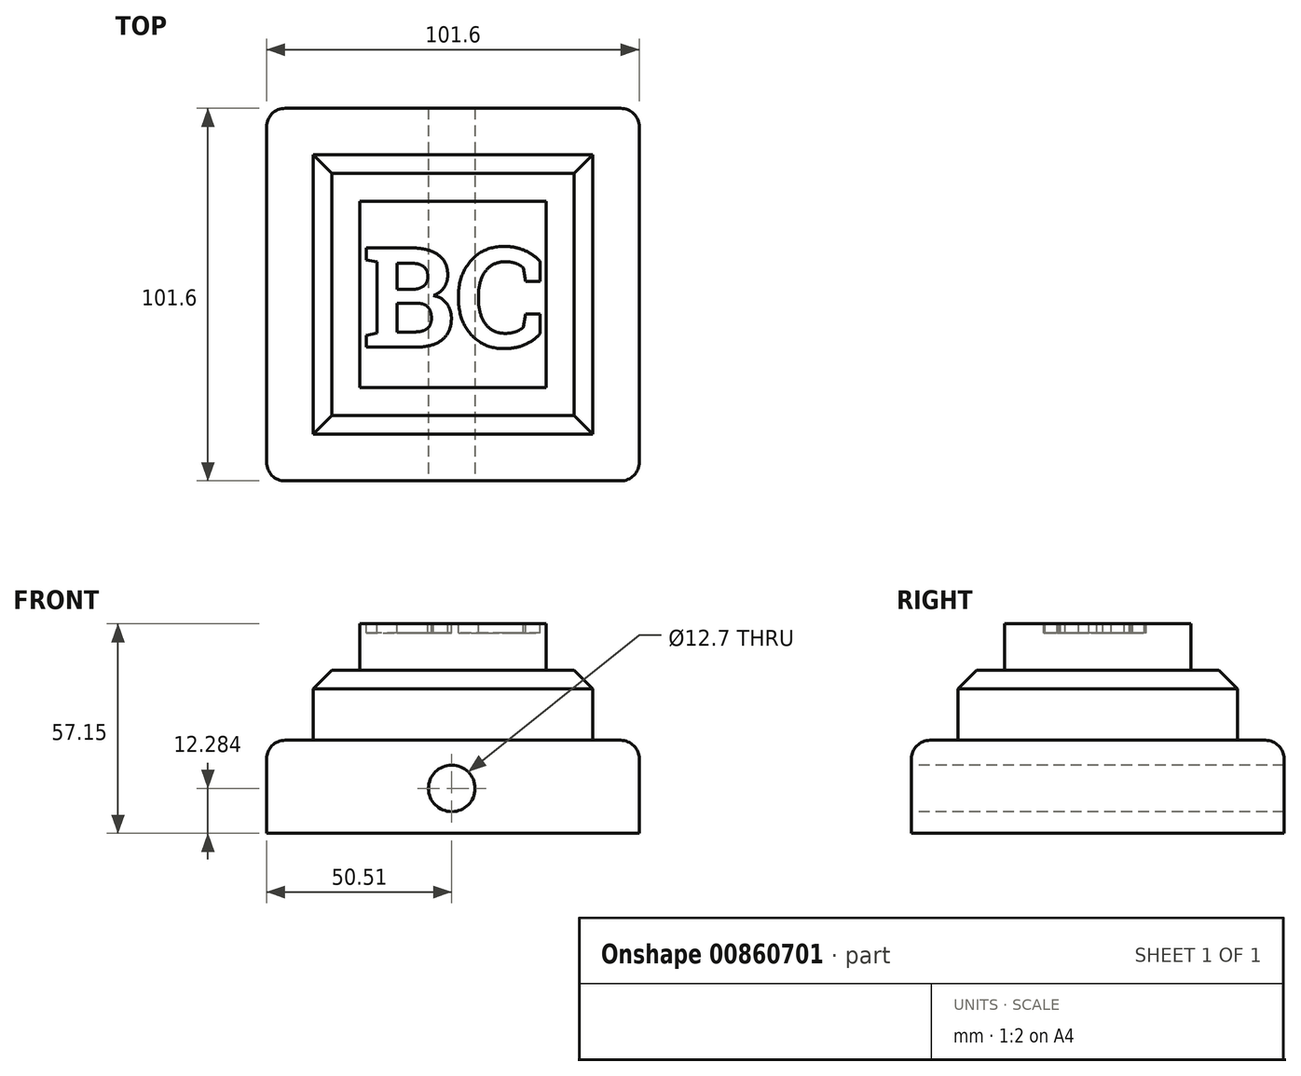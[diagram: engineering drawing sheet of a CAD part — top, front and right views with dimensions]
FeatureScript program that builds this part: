
annotation { "Feature Type Name" : "Feature", "Feature Type Description" : "" }
export const myFeature = defineFeature(function(context is Context, id is Id, definition is map)
    precondition{}
    {
        {
            var Q0;
            Q0=qCreatedBy(makeId("Top.planeOp"),FACE);
            var sketch = newSketch(context, id + "F0", { "sketchPlane" : qUnion([Q0])});
            skLineSegment(sketch, "E0.bottom", {"start": v(0, 0) * mm, "end": v(-101.6, 0) * mm});
            skLineSegment(sketch, "E0.top", {"start": v(0, 101.6) * mm, "end": v(-101.6, 101.6) * mm});
            skLineSegment(sketch, "E0.left", {"start": v(0, 0) * mm, "end": v(0, 101.6) * mm});
            skLineSegment(sketch, "E0.right", {"start": v(-101.6, 0) * mm, "end": v(-101.6, 101.6) * mm});
            skSolve(sketch);
        }
        {
            var Q0;
            Q0=makeQuery(id+"F0.imprint","IMPRINT",FACE,{"disambiguationData":[TD([[makeQuery(id+"F0.imprint","IMPRINT",EDGE,{"derivedFrom":sQuery(id+"F0.wireOp",EDGE,"E0.bottom")}),-1.0]])]});
            extrude(context, id + "F1", {"entities" : qUnion([Q0]), "depth" : 25.4 * mm, "offsetDistance" : 25.4 * mm});
        }
        {
            var Q0;
            Q0=makeQuery(id+"F1.opExtrude","CAP_FACE",FACE,{"disambiguationData":[OSD([sQuery(id+"F0.wireOp",EDGE,"E0.bottom"),sQuery(id+"F0.wireOp",EDGE,"E0.top"),sQuery(id+"F0.wireOp",EDGE,"E0.left"),sQuery(id+"F0.wireOp",EDGE,"E0.right")])],"isStart":false});
            var sketch = newSketch(context, id + "F2", { "sketchPlane" : qUnion([Q0])});
            skLineSegment(sketch, "E1.0", {"start": v(-12.7, 12.7) * mm, "end": v(-12.7, 88.9) * mm});
            skLineSegment(sketch, "E1.1", {"start": v(-88.9, 12.7) * mm, "end": v(-12.7, 12.7) * mm});
            skLineSegment(sketch, "E1.2", {"start": v(-88.9, 88.9) * mm, "end": v(-88.9, 12.7) * mm});
            skLineSegment(sketch, "E1.3", {"start": v(-12.7, 88.9) * mm, "end": v(-88.9, 88.9) * mm});
            skSolve(sketch);
        }
        {
            var Q0;
            Q0=makeQuery(id+"F2.imprint","IMPRINT",FACE,{"disambiguationData":[TD([[makeQuery(id+"F2.imprint","IMPRINT",EDGE,{"derivedFrom":sQuery(id+"F2.wireOp",EDGE,"E1.0")}),1.0]])]});
            extrude(context, id + "F3", {"entities" : qUnion([Q0]), "operationType" : NewBodyOperationType.ADD, "depth" : 19.05 * mm, "offsetDistance" : 25.4 * mm});
        }
        {
            var Q0;
            Q0=makeQuery(id+"F3.opExtrude","CAP_FACE",FACE,{"disambiguationData":[OSD([sQuery(id+"F2.wireOp",EDGE,"E1.0"),sQuery(id+"F2.wireOp",EDGE,"E1.1"),sQuery(id+"F2.wireOp",EDGE,"E1.2"),sQuery(id+"F2.wireOp",EDGE,"E1.3")])],"isStart":false});
            var sketch = newSketch(context, id + "F4", { "sketchPlane" : qUnion([Q0])});
            skLineSegment(sketch, "E2.0", {"start": v(-25.4, 76.2) * mm, "end": v(-76.2, 76.2) * mm});
            skLineSegment(sketch, "E2.1", {"start": v(-25.4, 25.4) * mm, "end": v(-25.4, 76.2) * mm});
            skLineSegment(sketch, "E2.2", {"start": v(-76.2, 25.4) * mm, "end": v(-25.4, 25.4) * mm});
            skLineSegment(sketch, "E2.3", {"start": v(-76.2, 76.2) * mm, "end": v(-76.2, 25.4) * mm});
            skSolve(sketch);
        }
        {
            var Q0;
            Q0=makeQuery(id+"F4.imprint","IMPRINT",FACE,{"disambiguationData":[TD([[makeQuery(id+"F4.imprint","IMPRINT",EDGE,{"derivedFrom":sQuery(id+"F4.wireOp",EDGE,"E2.0")}),1.0]])]});
            extrude(context, id + "F5", {"entities" : qUnion([Q0]), "operationType" : NewBodyOperationType.ADD, "depth" : 12.7 * mm, "offsetDistance" : 25.4 * mm});
        }
        {
            var Q0;
            Q0=makeQuery(id+"F1.opExtrude","SWEPT_FACE",FACE,{"disambiguationData":[OSD([sQuery(id+"F0.wireOp",EDGE,"E0.bottom")])]});
            var sketch = newSketch(context, id + "F6", { "sketchPlane" : qUnion([Q0])});
            skCircle(sketch, "E3", {"center": v(-51.09, 12.28) * mm, "radius": 6.35 * mm});
            skSolve(sketch);
        }
        {
            var Q0;
            Q0=makeQuery(id+"F6.imprint","IMPRINT",FACE,{"disambiguationData":[TD([[makeQuery(id+"F6.imprint","IMPRINT",EDGE,{"derivedFrom":sQuery(id+"F6.wireOp",EDGE,"E3")}),1.0]])]});
            extrude(context, id + "F7", {"entities" : qUnion([Q0]), "operationType" : NewBodyOperationType.REMOVE, "oppositeDirection" : true, "depth" : 101.6 * mm, "offsetDistance" : 25.4 * mm});
        }
        {
            var Q0;
            Q0=makeQuery(id+"F3.opExtrude","CAP_EDGE",EDGE,{"disambiguationData":[OSD([sQuery(id+"F2.wireOp",EDGE,"E1.1")])],"isStart":false});
            var Q1;
            Q1=makeQuery(id+"F3.opExtrude","CAP_EDGE",EDGE,{"disambiguationData":[OSD([sQuery(id+"F2.wireOp",EDGE,"E1.2")])],"isStart":false});
            var Q2;
            Q2=makeQuery(id+"F3.opExtrude","CAP_EDGE",EDGE,{"disambiguationData":[OSD([sQuery(id+"F2.wireOp",EDGE,"E1.0")])],"isStart":false});
            var Q3;
            Q3=makeQuery(id+"F3.opExtrude","CAP_EDGE",EDGE,{"disambiguationData":[OSD([sQuery(id+"F2.wireOp",EDGE,"E1.3")])],"isStart":false});
            chamfer(context, id + "F8", {"entities" : qUnion([Q0, Q1, Q2, Q3]), "width" : 5.08 * mm, "tangentPropagation" : true});
        }
        {
            var Q0;
            Q0=makeQuery(id+"F5.opExtrude","CAP_FACE",FACE,{"disambiguationData":[OSD([sQuery(id+"F4.wireOp",EDGE,"E2.0"),sQuery(id+"F4.wireOp",EDGE,"E2.1"),sQuery(id+"F4.wireOp",EDGE,"E2.2"),sQuery(id+"F4.wireOp",EDGE,"E2.3")])],"isStart":false});
            var sketch = newSketch(context, id + "F9", { "sketchPlane" : qUnion([Q0])});
            skText(sketch, "E4", { "text": "BC", "fontName": "RobotoSlab-Bold.ttf"});
            const initialGuessF9  = {"E4": [-0.07543, 0.03645, 1, 0, 0.02746]};
            skSetInitialGuess(sketch, initialGuessF9);
            skSolve(sketch);
        }
        {
            var Q0;
            Q0 = qSketchRegion(id + "F9", true);
            extrude(context, id + "F10", {"entities" : qUnion([Q0]), "operationType" : NewBodyOperationType.REMOVE, "oppositeDirection" : true, "depth" : 2.54 * mm, "offsetDistance" : 25.4 * mm});
        }
        {
            var Q0;
            Q0=makeQuery(id+"F1.opExtrude","CAP_EDGE",EDGE,{"disambiguationData":[OSD([sQuery(id+"F0.wireOp",EDGE,"E0.left")])],"isStart":false});
            var Q1;
            Q1=makeQuery(id+"F1.opExtrude","CAP_EDGE",EDGE,{"disambiguationData":[OSD([sQuery(id+"F0.wireOp",EDGE,"E0.bottom")])],"isStart":false});
            var Q2;
            Q2=makeQuery(id+"F1.opExtrude","CAP_EDGE",EDGE,{"disambiguationData":[OSD([sQuery(id+"F0.wireOp",EDGE,"E0.right")])],"isStart":false});
            var Q3;
            Q3=makeQuery(id+"F1.opExtrude","CAP_EDGE",EDGE,{"disambiguationData":[OSD([sQuery(id+"F0.wireOp",EDGE,"E0.top")])],"isStart":false});
            fillet(context, id + "F11", {"entities" : qUnion([Q0, Q1, Q2, Q3]), "radius" : 5.08 * mm, "tangentPropagation" : true, "allowEdgeOverflow" : false});
        }
        {
            var Q0;
            Q0=makeQuery(id+"F11.opFillet","BLEND_EDGE",EDGE,{"blendedFrom":[makeQuery(id+"F1.opExtrude","CAP_EDGE",EDGE,{"disambiguationData":[OSD([sQuery(id+"F0.wireOp",EDGE,"E0.bottom")])],"isStart":false}),makeQuery(id+"F1.opExtrude","CAP_EDGE",EDGE,{"disambiguationData":[OSD([sQuery(id+"F0.wireOp",EDGE,"E0.left")])],"isStart":false})],"blendedInto":[]});
            var Q1;
            Q1=makeQuery(id+"F11.opFillet","BLEND_EDGE",EDGE,{"blendedFrom":[makeQuery(id+"F1.opExtrude","CAP_EDGE",EDGE,{"disambiguationData":[OSD([sQuery(id+"F0.wireOp",EDGE,"E0.top")])],"isStart":false}),makeQuery(id+"F1.opExtrude","CAP_EDGE",EDGE,{"disambiguationData":[OSD([sQuery(id+"F0.wireOp",EDGE,"E0.left")])],"isStart":false})],"blendedInto":[]});
            var Q2;
            Q2=makeQuery(id+"F11.opFillet","BLEND_EDGE",EDGE,{"blendedFrom":[makeQuery(id+"F1.opExtrude","CAP_EDGE",EDGE,{"disambiguationData":[OSD([sQuery(id+"F0.wireOp",EDGE,"E0.bottom")])],"isStart":false}),makeQuery(id+"F1.opExtrude","CAP_EDGE",EDGE,{"disambiguationData":[OSD([sQuery(id+"F0.wireOp",EDGE,"E0.right")])],"isStart":false})],"blendedInto":[]});
            var Q3;
            Q3=makeQuery(id+"F11.opFillet","BLEND_FACE",FACE,{"disambiguationData":[OSD([sQuery(id+"F0.wireOp",EDGE,"E0.top")])]});
            fillet(context, id + "F12", {"entities" : qUnion([Q0, Q1, Q2, Q3]), "radius" : 5.08 * mm, "tangentPropagation" : true, "allowEdgeOverflow" : false});
        }
    });
